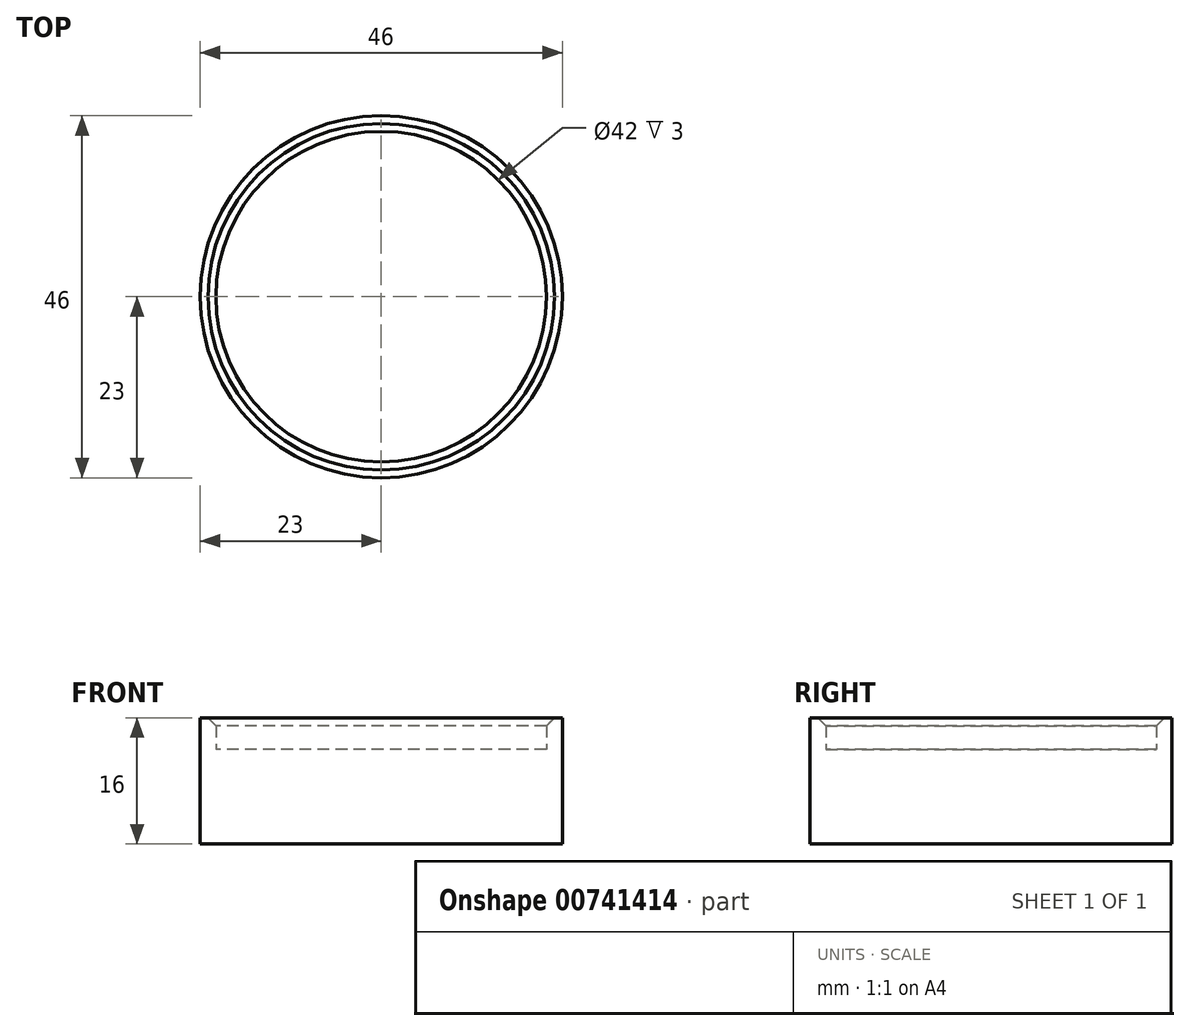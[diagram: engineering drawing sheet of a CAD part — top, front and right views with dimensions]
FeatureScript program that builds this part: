
annotation { "Feature Type Name" : "Feature", "Feature Type Description" : "" }
export const myFeature = defineFeature(function(context is Context, id is Id, definition is map)
    precondition{}
    {
        {
            var Q0;
            Q0=qCreatedBy(makeId("Top.planeOp"),FACE);
            var sketch = newSketch(context, id + "F0", { "sketchPlane" : qUnion([Q0])});
            skCircle(sketch, "E0", {"center": v(0, 0) * mm, "radius": 21 * mm});
            skSolve(sketch);
        }
        {
            var Q0;
            Q0 = qSketchRegion(id + "F0", true);
            extrude(context, id + "F1", {"entities" : qUnion([Q0]), "depth" : 12 * mm, "offsetDistance" : 25 * mm});
        }
        {
            var Q0;
            Q0=qCreatedBy(makeId("Top.planeOp"),FACE);
            var sketch = newSketch(context, id + "F2", { "sketchPlane" : qUnion([Q0])});
            skCircle(sketch, "E1", {"center": v(0, 0) * mm, "radius": 21 * mm});
            skCircle(sketch, "E2", {"center": v(0, 0) * mm, "radius": 23 * mm});
            skSolve(sketch);
        }
        {
            var Q0;
            Q0 = qSketchRegion(id + "F2", true);
            extrude(context, id + "F3", {"entities" : qUnion([Q0]), "operationType" : NewBodyOperationType.ADD, "depth" : 16 * mm, "offsetDistance" : 25 * mm});
        }
        {
            var Q0;
            Q0=makeQuery(id+"F3.opExtrude","CAP_EDGE",EDGE,{"disambiguationData":[OSD([sQuery(id+"F2.wireOp",EDGE,"E1")])],"isStart":false});
            chamfer(context, id + "F4", {"entities" : qUnion([Q0]), "width" : 1 * mm, "tangentPropagation" : true});
        }
    });
